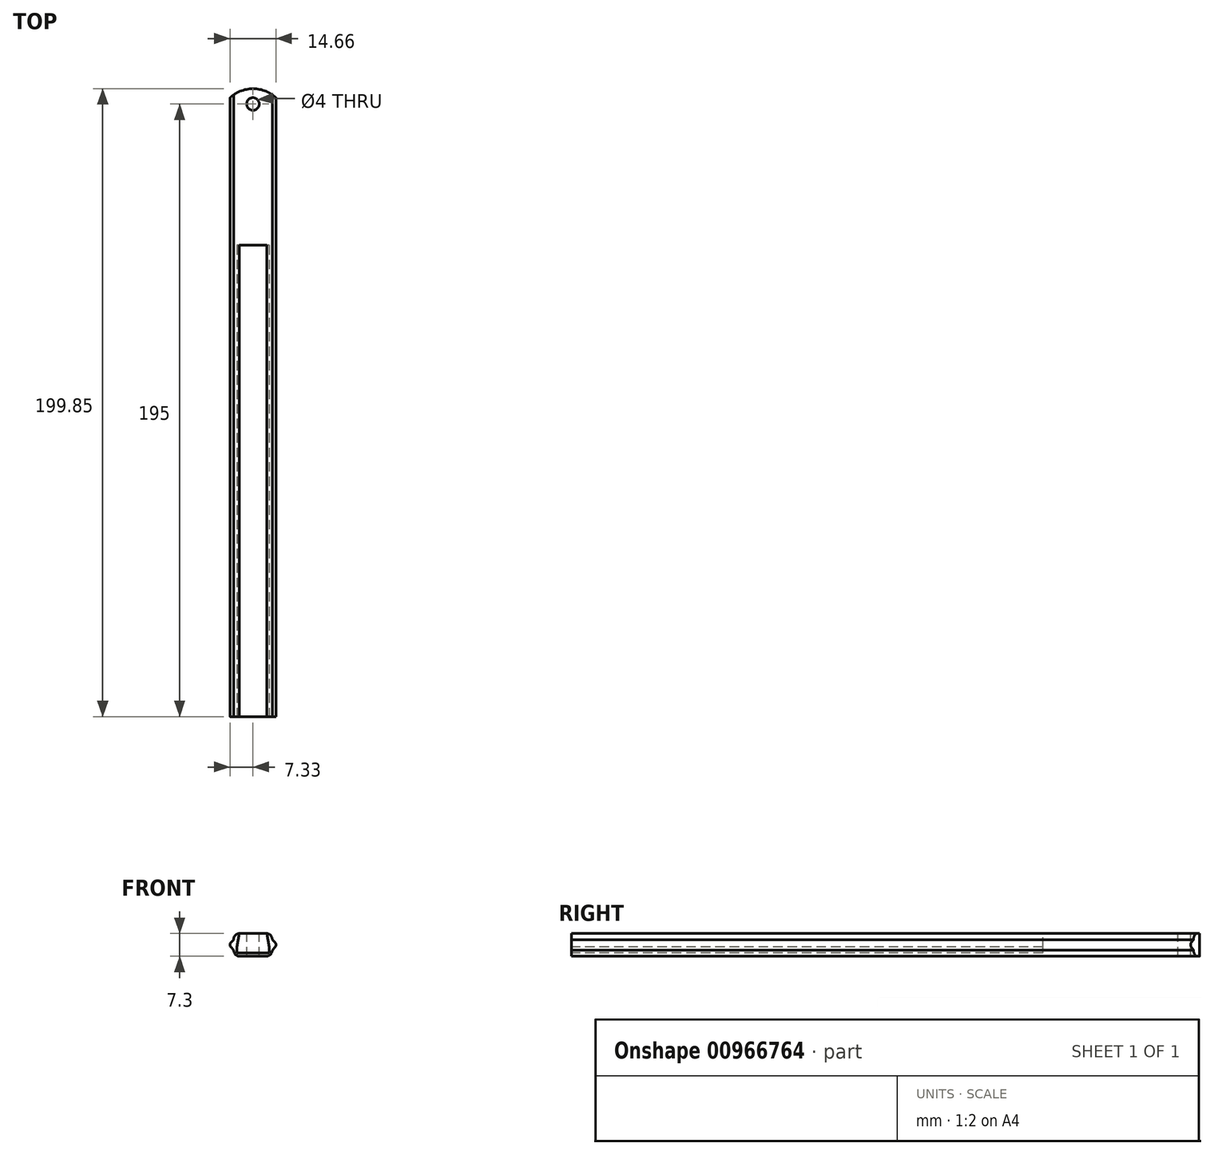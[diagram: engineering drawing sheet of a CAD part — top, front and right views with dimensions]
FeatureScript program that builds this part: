
annotation { "Feature Type Name" : "Feature", "Feature Type Description" : "" }
export const myFeature = defineFeature(function(context is Context, id is Id, definition is map)
    precondition{}
    {
        {
            var Q0;
            Q0=qCreatedBy(makeId("Front.planeOp"),FACE);
            var sketch = newSketch(context, id + "F0", { "sketchPlane" : qUnion([Q0])});
            skLineSegment(sketch, "E0.bottom", {"start": v(4.15, -2.65) * mm, "end": v(-4.15, -2.65) * mm});
            skLineSegment(sketch, "E0.top", {"start": v(4.15, 2.65) * mm, "end": v(-4.15, 2.65) * mm});
            skLineSegment(sketch, "E0.left", {"start": v(5.15, -1.65) * mm, "end": v(5.15, 1.65) * mm});
            skLineSegment(sketch, "E0.right", {"start": v(-5.15, -1.65) * mm, "end": v(-5.15, 1.65) * mm});
            skPoint(sketch, "E0.middle", {"position": v(0, 0) * mm});
            skPoint(sketch, "E1.visualSharp", {"position": v(-5.15, 2.65) * mm});
            skArc(sketch, "E1.filletArc", {"start": v(-4.15, 2.65) * mm, "mid": v(-4.86, 2.36) * mm, "end": v(-5.15, 1.65) * mm});
            skPoint(sketch, "E2.visualSharp", {"position": v(5.15, 2.65) * mm});
            skArc(sketch, "E2.filletArc", {"start": v(5.15, 1.65) * mm, "mid": v(4.86, 2.36) * mm, "end": v(4.15, 2.65) * mm});
            skPoint(sketch, "E3.visualSharp", {"position": v(5.15, -2.65) * mm});
            skArc(sketch, "E3.filletArc", {"start": v(4.15, -2.65) * mm, "mid": v(4.86, -2.36) * mm, "end": v(5.15, -1.65) * mm});
            skPoint(sketch, "E4.visualSharp", {"position": v(-5.15, -2.65) * mm});
            skArc(sketch, "E4.filletArc", {"start": v(-5.15, -1.65) * mm, "mid": v(-4.86, -2.36) * mm, "end": v(-4.15, -2.65) * mm});
            skArc(sketch, "E5.0", {"start": v(6.15, 1.65) * mm, "mid": v(5.56, 3.06) * mm, "end": v(4.15, 3.65) * mm});
            skLineSegment(sketch, "E5.2", {"start": v(4.15, 3.65) * mm, "end": v(-4.15, 3.65) * mm});
            skArc(sketch, "E5.3", {"start": v(4.15, -3.65) * mm, "mid": v(5.56, -3.06) * mm, "end": v(6.15, -1.65) * mm});
            skArc(sketch, "E5.4", {"start": v(-4.15, 3.65) * mm, "mid": v(-5.56, 3.06) * mm, "end": v(-6.15, 1.65) * mm});
            skArc(sketch, "E5.6", {"start": v(-6.15, -1.65) * mm, "mid": v(-5.56, -3.06) * mm, "end": v(-4.15, -3.65) * mm});
            skLineSegment(sketch, "E5.7", {"start": v(4.15, -3.65) * mm, "end": v(-4.15, -3.65) * mm});
            skLineSegment(sketch, "E6", {"start": v(-7.06, 0.69) * mm, "end": v(-6.15, 1.65) * mm});
            skLineSegment(sketch, "E7.MirrorCS", {"start": v(-7.06, -0.69) * mm, "end": v(-6.15, -1.65) * mm});
            skLineSegment(sketch, "E8.MirrorCS", {"start": v(7.06, 0.69) * mm, "end": v(6.15, 1.65) * mm});
            skLineSegment(sketch, "E9.MirrorCS", {"start": v(7.06, -0.69) * mm, "end": v(6.15, -1.65) * mm});
            skPoint(sketch, "E10.visualSharp", {"position": v(-7.7, 0) * mm});
            skArc(sketch, "E10.filletArc", {"start": v(-7.06, 0.69) * mm, "mid": v(-7.33, 0) * mm, "end": v(-7.06, -0.69) * mm});
            skPoint(sketch, "E11.visualSharp", {"position": v(7.7, 0) * mm});
            skArc(sketch, "E11.filletArc", {"start": v(7.06, -0.69) * mm, "mid": v(7.33, 0) * mm, "end": v(7.06, 0.69) * mm});
            skSolve(sketch);
        }
        {
            var Q0;
            Q0=makeQuery(id+"F0.imprint","IMPRINT",FACE,{"disambiguationData":[TD([[makeQuery(id+"F0.imprint","IMPRINT",EDGE,{"derivedFrom":sQuery(id+"F0.wireOp",EDGE,"E0.bottom")}),1.0]])]});
            var Q1;
            Q1=makeQuery(id+"F0.imprint","IMPRINT",FACE,{"disambiguationData":[TD([[makeQuery(id+"F0.imprint","IMPRINT",EDGE,{"derivedFrom":sQuery(id+"F0.wireOp",EDGE,"E0.bottom")}),-1.0]])]});
            extrude(context, id + "F1", {"entities" : qUnion([Q0, Q1]), "depth" : 200 * mm, "offsetDistance" : 25 * mm});
        }
        {
            var Q0;
            Q0=makeQuery(id+"F1.opExtrude","SWEPT_FACE",FACE,{"disambiguationData":[OSD([sQuery(id+"F0.wireOp",EDGE,"E5.2")])]});
            var sketch = newSketch(context, id + "F2", { "sketchPlane" : qUnion([Q0])});
            skCircle(sketch, "E12", {"center": v(0, -5) * mm, "radius": 2 * mm});
            skSolve(sketch);
        }
        {
            var Q0;
            Q0=makeQuery(id+"F2.imprint","IMPRINT",FACE,{"disambiguationData":[TD([[makeQuery(id+"F2.imprint","IMPRINT",EDGE,{"derivedFrom":sQuery(id+"F2.wireOp",EDGE,"S33YdpTx-NKYe-flyp-kQUo-xBa4HNO2xXOk")}),1.0]])]});
            var Q1;
            Q1=makeQuery(id+"F2.imprint","IMPRINT",FACE,{"disambiguationData":[TD([[makeQuery(id+"F2.imprint","IMPRINT",EDGE,{"derivedFrom":sQuery(id+"F2.wireOp",EDGE,"E12")}),1.0]])]});
            extrude(context, id + "F3", {"entities" : qUnion([Q0, Q1]), "operationType" : NewBodyOperationType.REMOVE, "endBound" : BoundingType.THROUGH_ALL, "oppositeDirection" : true, "depth" : 25 * mm, "offsetDistance" : 25 * mm});
        }
        {
            var Q0;
            Q0=qCreatedBy(makeId("Top.planeOp"),FACE);
            cPlane(context, id + "F4", {"entities" : qUnion([Q0]), "cplaneType" : CPlaneType.OFFSET, "offset" : 4.6 * mm, "width" : 150 * mm, "height" : 150 * mm});
        }
        {
            var Q0;
            Q0=qCreatedBy(id+"F4.planeOp",FACE);
            var sketch = newSketch(context, id + "F5", { "sketchPlane" : qUnion([Q0])});
            skLineSegment(sketch, "E13.bottom", {"start": v(8, 3.7) * mm, "end": v(-8, 3.7) * mm});
            skLineSegment(sketch, "E13.left", {"start": v(8, 3.7) * mm, "end": v(8, -3.7) * mm});
            skLineSegment(sketch, "E13.right", {"start": v(-8, 3.7) * mm, "end": v(-8, -3.7) * mm});
            skPoint(sketch, "E13.middle", {"position": v(0, 0) * mm});
            skArc(sketch, "E14", {"start": v(8, -3.7) * mm, "mid": v(0, -0.15) * mm, "end": v(-8, -3.7) * mm});
            skSolve(sketch);
        }
        {
            var Q0;
            Q0=makeQuery(id+"F5.imprint","IMPRINT",FACE,{"disambiguationData":[TD([[makeQuery(id+"F5.imprint","IMPRINT",EDGE,{"derivedFrom":sQuery(id+"F5.wireOp",EDGE,"E13.bottom")}),1.0]])]});
            extrude(context, id + "F6", {"entities" : qUnion([Q0]), "operationType" : NewBodyOperationType.REMOVE, "oppositeDirection" : true, "depth" : 25 * mm, "offsetDistance" : 25 * mm});
        }
        {
            var Q0;
            Q0=makeQuery(id+"F1.opExtrude","CAP_FACE",FACE,{"disambiguationData":[OSD([sQuery(id+"F0.wireOp",EDGE,"E0.bottom"),sQuery(id+"F0.wireOp",EDGE,"E0.top"),sQuery(id+"F0.wireOp",EDGE,"E0.left"),sQuery(id+"F0.wireOp",EDGE,"E0.right"),sQuery(id+"F0.wireOp",EDGE,"E1.filletArc"),sQuery(id+"F0.wireOp",EDGE,"E2.filletArc"),sQuery(id+"F0.wireOp",EDGE,"E3.filletArc"),sQuery(id+"F0.wireOp",EDGE,"E4.filletArc"),sQuery(id+"F0.wireOp",EDGE,"E5.0"),sQuery(id+"F0.wireOp",EDGE,"E5.2"),sQuery(id+"F0.wireOp",EDGE,"E5.3"),sQuery(id+"F0.wireOp",EDGE,"E5.4"),sQuery(id+"F0.wireOp",EDGE,"E5.6"),sQuery(id+"F0.wireOp",EDGE,"E5.7"),sQuery(id+"F0.wireOp",EDGE,"E6"),sQuery(id+"F0.wireOp",EDGE,"E7.MirrorCS"),sQuery(id+"F0.wireOp",EDGE,"E8.MirrorCS"),sQuery(id+"F0.wireOp",EDGE,"E9.MirrorCS"),sQuery(id+"F0.wireOp",EDGE,"E10.filletArc"),sQuery(id+"F0.wireOp",EDGE,"E11.filletArc")])],"isStart":false});
            cPlane(context, id + "F7", {"entities" : qUnion([Q0]), "cplaneType" : CPlaneType.OFFSET, "offset" : 0 * mm, "width" : 150 * mm, "height" : 150 * mm});
        }
        {
            var Q0;
            Q0=qCreatedBy(id+"F7.planeOp",FACE);
            var sketch = newSketch(context, id + "F8", { "sketchPlane" : qUnion([Q0])});
            skLineSegment(sketch, "E15", {"start": v(0, -2.65) * mm, "end": v(5.13, -2.65) * mm});
            skLineSegment(sketch, "E16", {"start": v(5.13, -2.65) * mm, "end": v(5.13, -0.66) * mm});
            skLineSegment(sketch, "E17", {"start": v(5.13, -0.66) * mm, "end": v(4.39, 3.75) * mm});
            skLineSegment(sketch, "E18", {"start": v(4.39, 3.75) * mm, "end": v(0, 3.75) * mm});
            skLineSegment(sketch, "E19.MirrorCS", {"start": v(-4.39, 3.75) * mm, "end": v(0, 3.75) * mm});
            skLineSegment(sketch, "E20.MirrorCS", {"start": v(-5.13, -0.66) * mm, "end": v(-4.39, 3.75) * mm});
            skLineSegment(sketch, "E21.MirrorCS", {"start": v(-5.13, -2.65) * mm, "end": v(-5.13, -0.66) * mm});
            skLineSegment(sketch, "E22.MirrorCS", {"start": v(0, -2.65) * mm, "end": v(-5.13, -2.65) * mm});
            skSolve(sketch);
        }
        {
            var Q0;
            Q0=makeQuery(id+"F8.imprint","IMPRINT",FACE,{"disambiguationData":[TD([[makeQuery(id+"F8.imprint","IMPRINT",EDGE,{"derivedFrom":sQuery(id+"F8.wireOp",EDGE,"E15")}),1.0]])]});
            extrude(context, id + "F9", {"entities" : qUnion([Q0]), "operationType" : NewBodyOperationType.REMOVE, "oppositeDirection" : true, "depth" : 150 * mm, "offsetDistance" : 25 * mm});
        }
    });
